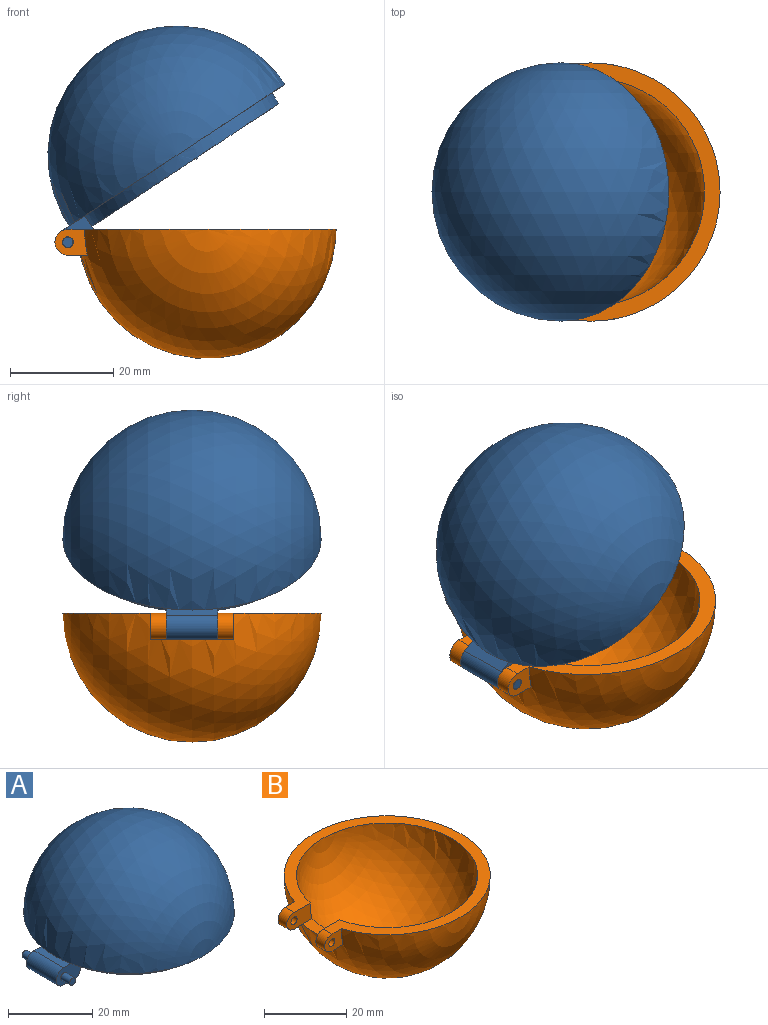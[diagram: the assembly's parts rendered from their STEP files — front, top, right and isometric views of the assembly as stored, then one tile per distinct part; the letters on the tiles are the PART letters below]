
ASSEMBLY  parts=2 mates=1
PART A: 17 faces, bbox 54.4x50x47 mm
  f0: plane 8x5mm, normal (0,1,0), area 33.7mm2, adj f3,f5,f6,f7,f13,f15,f16
  f1: plane 8x5mm, normal (0,-1,0), area 33.7mm2, adj f3,f5,f6,f7,f12,f15,f16
  f2: sphere r=22mm, area 362.8mm2, adj f3,f5,f8,f9
  f3: plane 50x49.5mm, normal (0,0,-1), area 412.7mm2, adj f0,f1,f2,f4
  f4: sphere r=25mm, area 3927mm2, adj f3,f7
  f5: cylinder r=22mm len=10mm, axis (0,0,1), area 35.3mm2, adj f0,f1,f2,f16
  f6: plane 10x3.96mm, normal (0,0,-1), area 36mm2, adj f0,f1,f15,f16
  f7: plane 10x2.43mm, normal (0,0,1), area 20.9mm2, adj f0,f1,f4,f15
  f8: plane 8.66x2.5mm, normal (1,0,0), area 15.4mm2, adj f2,f9
  f9: plane 43.72x43.28mm, normal (0,0,-1), area 383.9mm2, adj f2,f8,f10
  f10: sphere r=19mm, area 2566.4mm2, adj f9
  f11: plane 2x2mm, normal (0,-1,0), area 3.1mm2, adj f12
  f12: cylinder r=1mm len=3mm, axis (0,1,0), area 18.8mm2, adj f1,f11
  f13: cylinder r=1mm len=3mm, axis (0,1,0), area 18.8mm2, adj f0,f14
  f14: plane 2x2mm, normal (0,1,0), area 3.1mm2, adj f13
  f15: cylinder r=2.5mm len=10mm, axis (0,-1,0), area 78.5mm2, adj f0,f1,f6,f7
  f16: torus R=23.5mm, axis (0,0,-1), area 23.8mm2, adj f0,f1,f5,f6
PART B: 14 faces, bbox 54.4x50x25 mm
  f0: plane 8.59x5mm, normal (0,-1,0), area 34.8mm2, adj f3,f6,f7,f8,f11,f12
  f1: plane 8.59x5mm, normal (0,1,0), area 34.8mm2, adj f4,f6,f7,f8,f10,f13
  f2: plane 6.27x5mm, normal (0,1,0), area 23.4mm2, adj f3,f5,f7,f11,f12
  f3: plane 3.77x3mm, normal (0,0,-1), area 10mm2, adj f0,f2,f5,f12
  f4: plane 3.77x3mm, normal (0,0,-1), area 10mm2, adj f1,f5,f9,f13
  f5: sphere r=25mm, area 3845mm2, adj f2,f3,f4,f7,f8,f9
  f6: sphere r=22mm, area 2990.2mm2, adj f0,f1,f7,f8
  f7: plane 51.92x50mm, normal (0,0,1), area 429.5mm2, adj f0,f1,f2,f5,f6,f9,f12,f13
  f8: plane 10x3.66mm, normal (0,0,1), area 31mm2, adj f0,f1,f5,f6
  f9: plane 6.27x5mm, normal (0,-1,0), area 23.4mm2, adj f4,f5,f7,f10,f13
  f10: cylinder r=1.05mm len=3mm, axis (0,-1,0), area 19.8mm2, adj f1,f9
  f11: cylinder r=1.05mm len=3mm, axis (0,-1,0), area 19.8mm2, adj f0,f2
  f12: cylinder r=2.5mm len=5mm, axis (0,-1,0), area 23.6mm2, adj f0,f2,f3,f7
  f13: cylinder r=2.5mm len=5mm, axis (0,-1,0), area 23.6mm2, adj f1,f4,f7,f9
PLACE A rot(axis=(0,-1,0),33.3deg) t=(-2.85,-2,23.24)mm
PLACE B t=(2.95,-2,8.87)mm fixed
MATE revolute A.f12 <-> B.f10  axis (0,-1,0) through (-23.98,-10,6.37)mm
